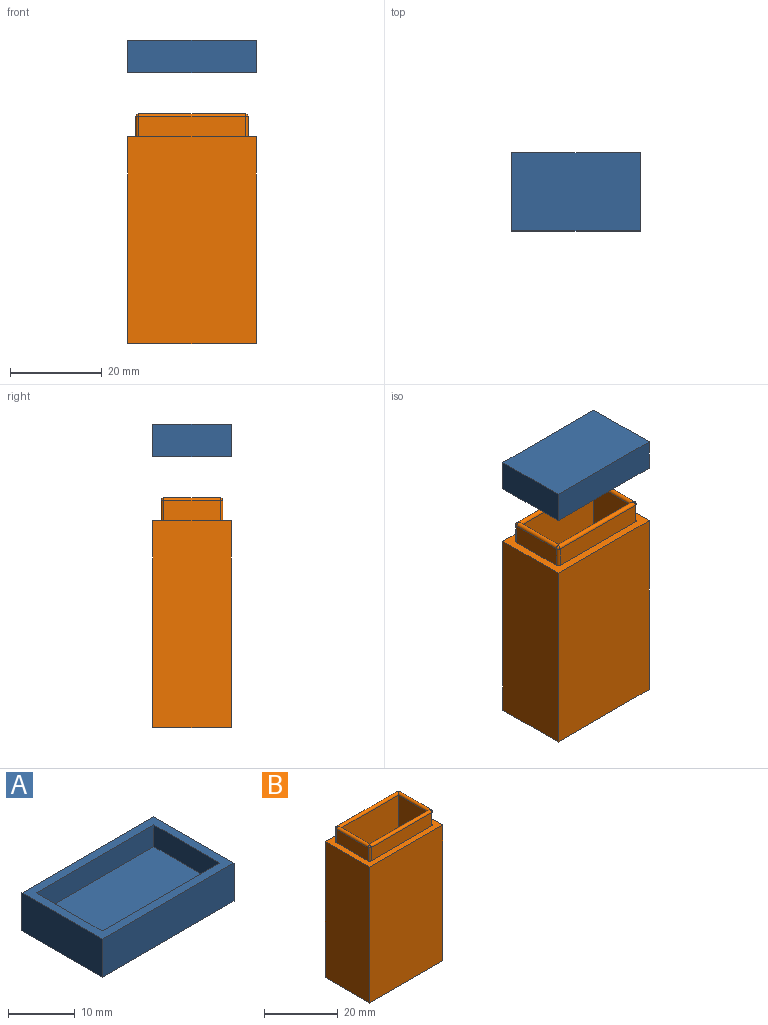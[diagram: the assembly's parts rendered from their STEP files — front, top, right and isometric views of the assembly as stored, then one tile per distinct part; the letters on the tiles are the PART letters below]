
ASSEMBLY  parts=2 mates=1
PART A: 11 faces, bbox 28x17x7 mm
  f0: plane 28x17mm, normal (0,0,-1), area 476mm2, adj f5,f6,f7,f8
  f1: plane 25x4mm, normal (0,-1,0), area 100mm2, adj f2,f4,f9,f10
  f2: plane 14x4mm, normal (1,0,0), area 56mm2, adj f1,f3,f9,f10
  f3: plane 25x4mm, normal (0,1,0), area 100mm2, adj f2,f4,f9,f10
  f4: plane 14x4mm, normal (-1,0,0), area 56mm2, adj f1,f3,f9,f10
  f5: plane 17x7mm, normal (-1,0,0), area 119mm2, adj f0,f6,f8,f9
  f6: plane 28x7mm, normal (0,-1,0), area 196mm2, adj f0,f5,f7,f9
  f7: plane 17x7mm, normal (1,0,0), area 119mm2, adj f0,f6,f8,f9
  f8: plane 28x7mm, normal (0,1,0), area 196mm2, adj f0,f5,f7,f9
  f9: plane 28x17mm, normal (0,0,1), area 126mm2, adj f1,f2,f3,f4,f5,f6,f7,f8
  f10: plane 25x14mm, normal (0,0,1), area 350mm2, adj f1,f2,f3,f4
PART B: 27 faces, bbox 28x17x50 mm
  f0: plane 46.4x11mm, normal (1,0,0), area 510.4mm2, adj f1,f3,f8,f22
  f1: plane 46.4x22mm, normal (0,1,0), area 1020.8mm2, adj f0,f2,f8,f23
  f2: plane 46.4x11mm, normal (-1,0,0), area 510.4mm2, adj f1,f3,f8,f19
  f3: plane 46.4x22mm, normal (0,-1,0), area 1020.8mm2, adj f0,f2,f8,f18
  f4: plane 12.2x4.4mm, normal (-1,0,0), area 53.7mm2, adj f13,f17,f22,f26
  f5: plane 23.2x4.4mm, normal (0,-1,0), area 102.1mm2, adj f13,f20,f23,f26
  f6: plane 12.2x4.4mm, normal (1,0,0), area 53.7mm2, adj f13,f15,f19,f20
  f7: plane 23.2x4.4mm, normal (0,1,0), area 102.1mm2, adj f13,f15,f17,f18
  f8: plane 22x11mm, normal (0,0,1), area 242mm2, adj f0,f1,f2,f3
  f9: plane 45x17mm, normal (-1,0,0), area 765mm2, adj f10,f12,f13,f14
  f10: plane 45x28mm, normal (0,-1,0), area 1260mm2, adj f9,f11,f13,f14
  f11: plane 45x17mm, normal (1,0,0), area 765mm2, adj f10,f12,f13,f14
  f12: plane 45x28mm, normal (0,1,0), area 1260mm2, adj f9,f11,f13,f14
  f13: plane 28x17mm, normal (0,0,1), area 149.3mm2, adj f4,f5,f6,f7,f9,f10,f11,f12
  f14: plane 28x17mm, normal (0,0,-1), area 476mm2, adj f9,f10,f11,f12
  f15: cylinder r=0.6mm len=4.4mm, axis (0,0,1), area 4.1mm2, adj f6,f7,f13,f16
  f16: sphere r=0.6mm, area 0.6mm2, adj f15,f18,f19
  f17: cylinder r=0.6mm len=4.4mm, axis (0,0,-1), area 4.1mm2, adj f4,f7,f13,f21
  f18: cylinder r=0.6mm len=23.2mm, axis (1,0,0), area 43mm2, adj f3,f7,f16,f19,f21,f22
  f19: cylinder r=0.6mm len=12.2mm, axis (0,1,0), area 22.3mm2, adj f2,f6,f16,f18,f23,f24
  f20: cylinder r=0.6mm len=4.4mm, axis (0,0,-1), area 4.1mm2, adj f5,f6,f13,f24
  f21: sphere r=0.6mm, area 0.6mm2, adj f17,f18,f22
  f22: cylinder r=0.6mm len=12.2mm, axis (0,-1,0), area 22.3mm2, adj f0,f4,f18,f21,f23,f25
  f23: cylinder r=0.6mm len=23.2mm, axis (1,0,0), area 43mm2, adj f1,f5,f19,f22,f24,f25
  f24: sphere r=0.6mm, area 0.6mm2, adj f19,f20,f23
  f25: sphere r=0.6mm, area 0.6mm2, adj f22,f23,f26
  f26: cylinder r=0.6mm len=4.4mm, axis (0,0,1), area 4.1mm2, adj f4,f5,f13,f25
PLACE A rot(axis=(1,0,0),180deg) t=(0,44,66)mm
PLACE B at identity
MATE slider B.f8 <-> A.f10  axis (0,0,1) through (14,8.5,3)mm
